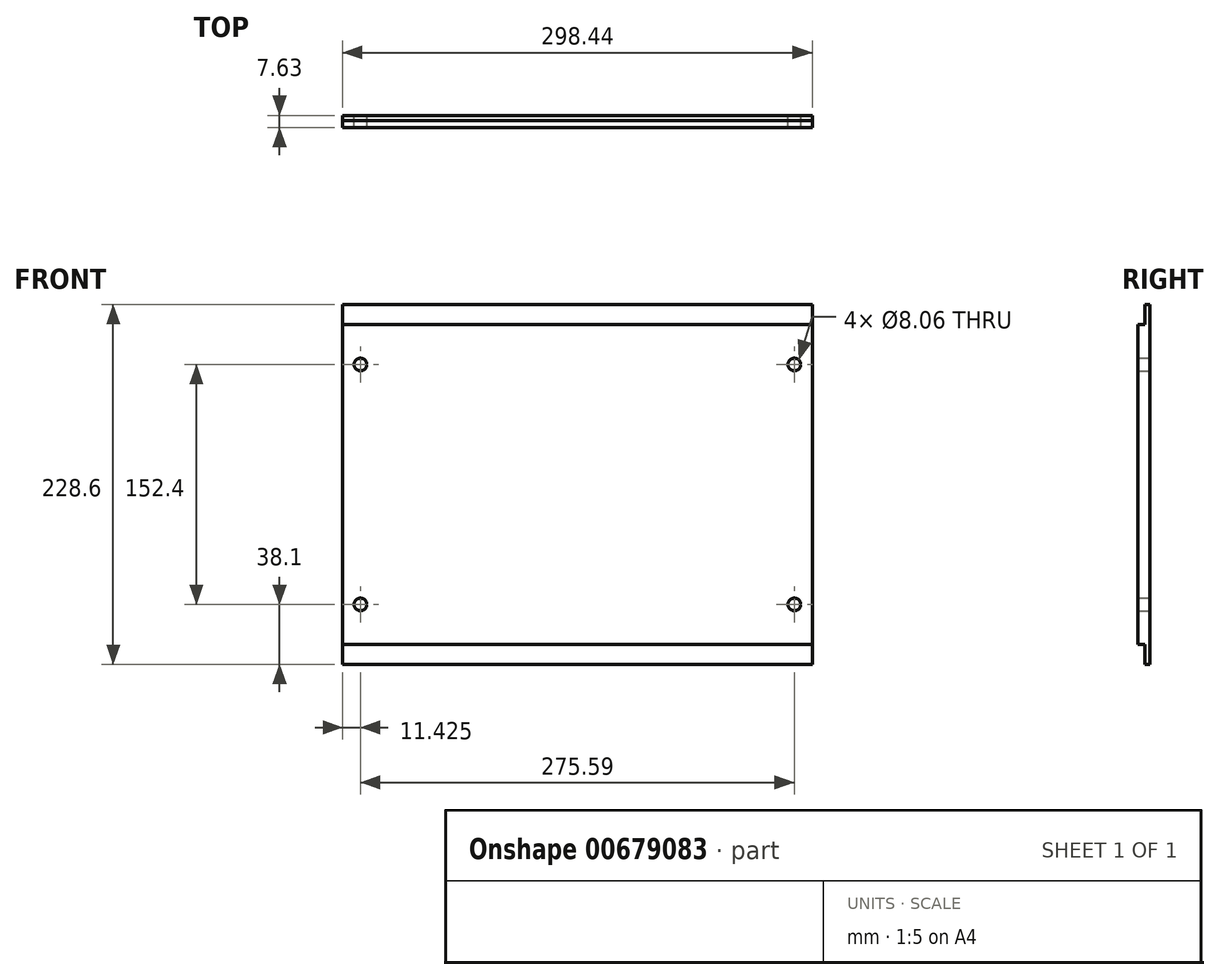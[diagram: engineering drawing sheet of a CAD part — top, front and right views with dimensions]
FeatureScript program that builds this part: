
annotation { "Feature Type Name" : "Feature", "Feature Type Description" : "" }
export const myFeature = defineFeature(function(context is Context, id is Id, definition is map)
    precondition{}
    {
        {
            var Q0;
            Q0=qCreatedBy(makeId("Front.planeOp"),FACE);
            var sketch = newSketch(context, id + "F0", { "sketchPlane" : qUnion([Q0])});
            skLineSegment(sketch, "E0.bottom", {"start": v(-149.22, 114.3) * mm, "end": v(149.23, 114.3) * mm});
            skLineSegment(sketch, "E0.top", {"start": v(-149.23, -114.3) * mm, "end": v(149.22, -114.3) * mm});
            skLineSegment(sketch, "E0.left", {"start": v(-149.22, 114.3) * mm, "end": v(-149.23, -114.3) * mm});
            skLineSegment(sketch, "E0.right", {"start": v(149.23, 114.3) * mm, "end": v(149.22, -114.3) * mm});
            skLineSegment(sketch, "E1.bottom", {"start": v(-149.23, 101.6) * mm, "end": v(149.23, 101.6) * mm});
            skLineSegment(sketch, "E1.top", {"start": v(-149.23, -101.6) * mm, "end": v(149.23, -101.6) * mm});
            skLineSegment(sketch, "E1.left", {"start": v(-149.23, 101.6) * mm, "end": v(-149.23, -101.6) * mm});
            skLineSegment(sketch, "E1.right", {"start": v(149.23, 101.6) * mm, "end": v(149.23, -101.6) * mm});
            skCircle(sketch, "E2", {"center": v(137.8, -76.2) * mm, "radius": 4.03 * mm});
            skCircle(sketch, "E3", {"center": v(137.8, 76.2) * mm, "radius": 4.03 * mm});
            skCircle(sketch, "E4", {"center": v(-137.8, 76.2) * mm, "radius": 4.03 * mm});
            skCircle(sketch, "E5", {"center": v(-137.8, -76.2) * mm, "radius": 4.03 * mm});
            skSolve(sketch);
        }
        {
            var Q0;
            Q0=makeQuery(id+"F0.imprint","IMPRINT",FACE,{"disambiguationData":[TD([[makeQuery(id+"F0.imprint","IMPRINT",EDGE,{"derivedFrom":sQuery(id+"F0.wireOp",EDGE,"E1.bottom")}),-1.0]])]});
            extrude(context, id + "F1", {"entities" : qUnion([Q0]), "depth" : 4.44 * mm, "offsetDistance" : 25.4 * mm});
        }
        {
            var Q0;
            Q0=makeQuery(id+"F0.imprint","IMPRINT",FACE,{"disambiguationData":[TD([[makeQuery(id+"F0.imprint","IMPRINT",EDGE,{"derivedFrom":sQuery(id+"F0.wireOp",EDGE,"E0.bottom")}),-1.0]])]});
            var Q1;
            Q1=makeQuery(id+"F0.imprint","IMPRINT",FACE,{"disambiguationData":[TD([[makeQuery(id+"F0.imprint","IMPRINT",EDGE,{"derivedFrom":sQuery(id+"F0.wireOp",EDGE,"E1.bottom")}),-1.0]])]});
            var Q2;
            {var subQ0=sQuery(id+"F0.wireOp",EDGE,"E0.top");Q2=makeQuery(id+"F0.imprint","IMPRINT",FACE,{"disambiguationData":[TD([[makeQuery(id+"F0.imprint","IMPRINT",EDGE,{"derivedFrom":subQ0}),1.0]])]});}
            extrude(context, id + "F2", {"entities" : qUnion([Q0, Q1, Q2]), "operationType" : NewBodyOperationType.ADD, "depth" : -3.17 * mm, "offsetDistance" : 25.4 * mm});
        }
    });
